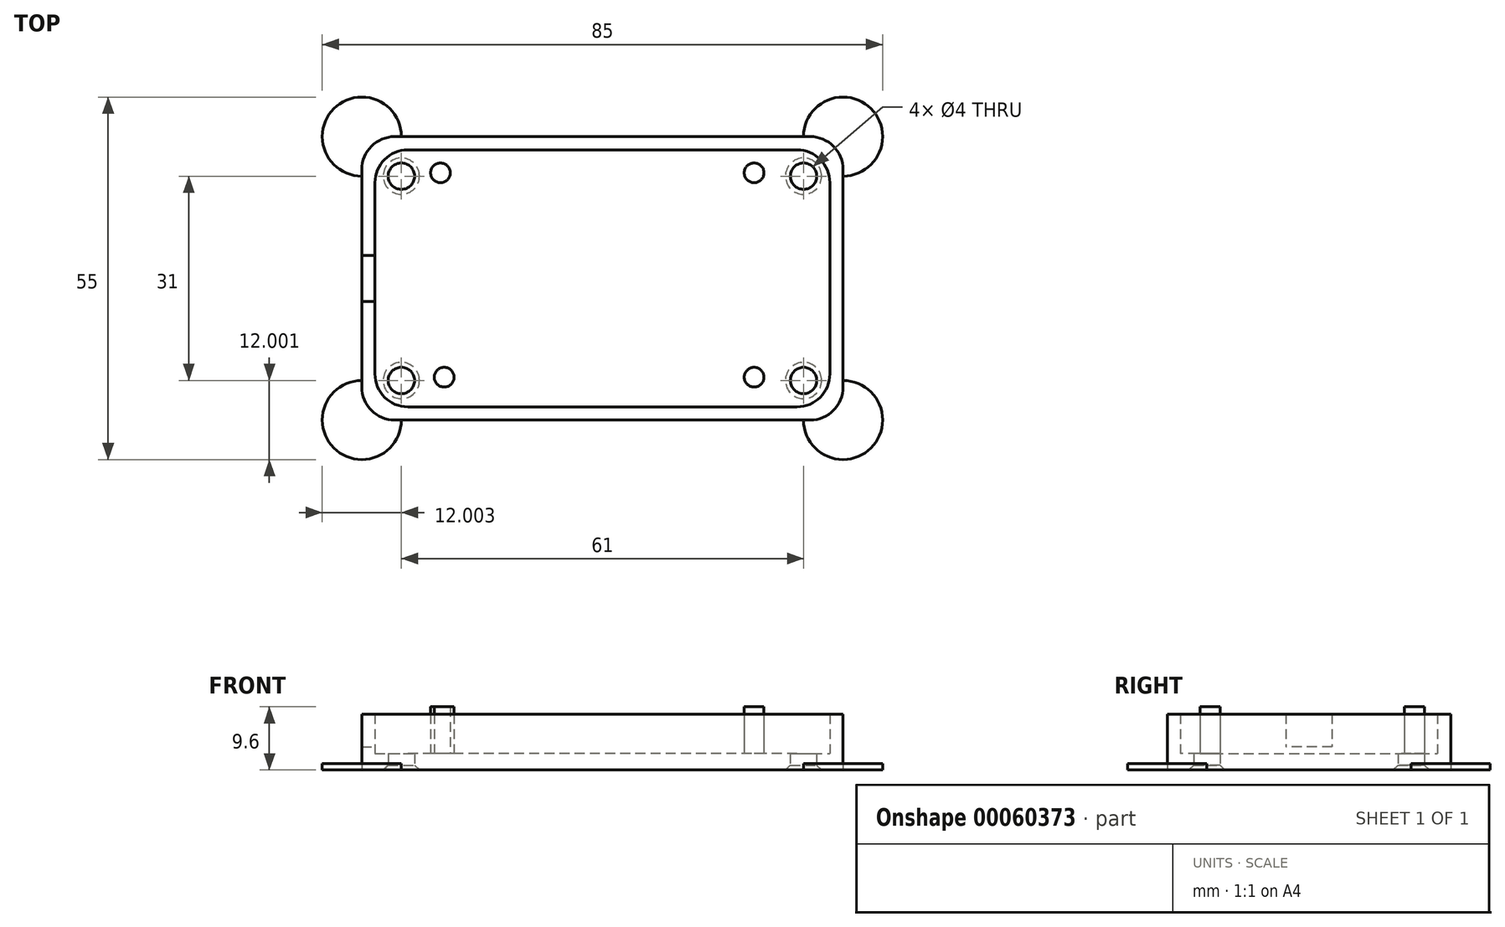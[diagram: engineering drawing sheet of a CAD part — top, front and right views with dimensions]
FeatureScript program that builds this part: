
annotation { "Feature Type Name" : "Feature", "Feature Type Description" : "" }
export const myFeature = defineFeature(function(context is Context, id is Id, definition is map)
    precondition{}
    {
        {
            var Q0;
            Q0=qCreatedBy(makeId("Top.planeOp"),FACE);
            var sketch = newSketch(context, id + "F0", { "sketchPlane" : qUnion([Q0])});
            skLineSegment(sketch, "E0.bottom", {"start": v(-6.76, 68.41) * mm, "end": v(52.24, 68.41) * mm});
            skLineSegment(sketch, "E0.top", {"start": v(-6.76, 29.41) * mm, "end": v(52.24, 29.41) * mm});
            skLineSegment(sketch, "E0.left", {"start": v(-11.76, 63.41) * mm, "end": v(-11.76, 34.41) * mm});
            skLineSegment(sketch, "E0.right", {"start": v(57.24, 63.41) * mm, "end": v(57.24, 34.41) * mm});
            skCircle(sketch, "E1", {"center": v(-7.76, 64.41) * mm, "radius": 1.5 * mm, "construction": true});
            skCircle(sketch, "E2", {"center": v(-7.76, 33.41) * mm, "radius": 1.5 * mm, "construction": true});
            skCircle(sketch, "E3", {"center": v(53.24, 64.41) * mm, "radius": 1.5 * mm, "construction": true});
            skCircle(sketch, "E4", {"center": v(53.24, 33.41) * mm, "radius": 1.5 * mm, "construction": true});
            skCircle(sketch, "E5.0", {"center": v(53.24, 33.41) * mm, "radius": 2 * mm});
            skCircle(sketch, "E6.0", {"center": v(53.24, 64.41) * mm, "radius": 2 * mm});
            skCircle(sketch, "E7.0", {"center": v(-7.76, 64.41) * mm, "radius": 2 * mm});
            skCircle(sketch, "E8.0", {"center": v(-7.76, 33.41) * mm, "radius": 2 * mm});
            skPoint(sketch, "E9", {"position": v(-1.26, 33.91) * mm});
            skLineSegment(sketch, "E10.0", {"start": v(-13.76, 65.41) * mm, "end": v(-13.76, 32.41) * mm});
            skLineSegment(sketch, "E10.1", {"start": v(-8.76, 70.41) * mm, "end": v(54.24, 70.41) * mm});
            skLineSegment(sketch, "E10.2", {"start": v(59.24, 65.41) * mm, "end": v(59.24, 32.41) * mm});
            skLineSegment(sketch, "E10.3", {"start": v(-8.76, 27.41) * mm, "end": v(54.24, 27.41) * mm});
            skPoint(sketch, "E11", {"position": v(-13.76, 52.41) * mm});
            skPoint(sketch, "E12", {"position": v(-13.76, 45.41) * mm});
            skLineSegment(sketch, "E13", {"start": v(-13.76, 52.41) * mm, "end": v(-11.76, 52.41) * mm});
            skLineSegment(sketch, "E14", {"start": v(-13.76, 45.41) * mm, "end": v(-11.76, 45.41) * mm});
            skPoint(sketch, "E15", {"position": v(-1.82, 64.91) * mm});
            skPoint(sketch, "E16", {"position": v(45.74, 33.91) * mm});
            skPoint(sketch, "E17", {"position": v(45.74, 64.91) * mm});
            skCircle(sketch, "E18", {"center": v(-1.26, 33.91) * mm, "radius": 1.5 * mm});
            skCircle(sketch, "E19", {"center": v(-1.82, 64.91) * mm, "radius": 1.5 * mm});
            skCircle(sketch, "E20", {"center": v(45.74, 64.91) * mm, "radius": 1.5 * mm});
            skCircle(sketch, "E21", {"center": v(45.74, 33.91) * mm, "radius": 1.5 * mm});
            skArc(sketch, "E22", {"start": v(59.24, 64.41) * mm, "mid": v(63.49, 74.65) * mm, "end": v(53.24, 70.41) * mm});
            skArc(sketch, "E23", {"start": v(53.24, 27.41) * mm, "mid": v(63.49, 23.17) * mm, "end": v(59.24, 33.41) * mm});
            skArc(sketch, "E24", {"start": v(-7.76, 70.41) * mm, "mid": v(-18, 74.65) * mm, "end": v(-13.76, 64.41) * mm});
            skArc(sketch, "E25", {"start": v(-13.76, 33.41) * mm, "mid": v(-18, 23.17) * mm, "end": v(-7.76, 27.41) * mm});
            skPoint(sketch, "E26.visualSharp", {"position": v(57.24, 68.41) * mm});
            skArc(sketch, "E26.filletArc", {"start": v(57.24, 63.41) * mm, "mid": v(55.78, 66.95) * mm, "end": v(52.24, 68.41) * mm});
            skArc(sketch, "E27.filletArc", {"start": v(59.24, 65.41) * mm, "mid": v(57.78, 68.95) * mm, "end": v(54.24, 70.41) * mm});
            skPoint(sketch, "E28.visualSharp", {"position": v(-11.76, 68.41) * mm});
            skArc(sketch, "E28.filletArc", {"start": v(-6.76, 68.41) * mm, "mid": v(-10.3, 66.95) * mm, "end": v(-11.76, 63.41) * mm});
            skArc(sketch, "E29.filletArc", {"start": v(-8.76, 70.41) * mm, "mid": v(-12.3, 68.95) * mm, "end": v(-13.76, 65.41) * mm});
            skPoint(sketch, "E30.visualSharp", {"position": v(-11.76, 29.41) * mm});
            skArc(sketch, "E30.filletArc", {"start": v(-11.76, 34.41) * mm, "mid": v(-10.3, 30.88) * mm, "end": v(-6.76, 29.41) * mm});
            skArc(sketch, "E31.filletArc", {"start": v(-13.76, 32.41) * mm, "mid": v(-12.3, 28.88) * mm, "end": v(-8.76, 27.41) * mm});
            skPoint(sketch, "E32.visualSharp", {"position": v(57.24, 29.41) * mm});
            skArc(sketch, "E32.filletArc", {"start": v(52.24, 29.41) * mm, "mid": v(55.78, 30.88) * mm, "end": v(57.24, 34.41) * mm});
            skArc(sketch, "E33.filletArc", {"start": v(54.24, 27.41) * mm, "mid": v(57.78, 28.88) * mm, "end": v(59.24, 32.41) * mm});
            skSolve(sketch);
        }
        {
            var Q0;
            {var subQ0=sQuery(id+"F0.wireOp",EDGE,"E0.bottom");Q0=makeQuery(id+"F0.imprint","IMPRINT",FACE,{"disambiguationData":[TD([[makeQuery(id+"F0.imprint","IMPRINT",EDGE,{"derivedFrom":subQ0}),-1.0]])]});}
            var Q1;
            {var subQ5=sQuery(id+"F0.wireOp",EDGE,"E0.bottom");Q1=makeQuery(id+"F0.imprint","IMPRINT",FACE,{"disambiguationData":[TD([[makeQuery(id+"F0.imprint","IMPRINT",EDGE,{"derivedFrom":subQ5}),1.0]])]});}
            var Q2;
            Q2=makeQuery(id+"F0.imprint","IMPRINT",FACE,{"disambiguationData":[TD([[makeQuery(id+"F0.imprint","IMPRINT",EDGE,{"derivedFrom":sQuery(id+"F0.wireOp",EDGE,"E18")}),1.0]])]});
            var Q3;
            Q3=makeQuery(id+"F0.imprint","IMPRINT",FACE,{"disambiguationData":[TD([[makeQuery(id+"F0.imprint","IMPRINT",EDGE,{"derivedFrom":sQuery(id+"F0.wireOp",EDGE,"E21")}),1.0]])]});
            var Q4;
            Q4=makeQuery(id+"F0.imprint","IMPRINT",FACE,{"disambiguationData":[TD([[makeQuery(id+"F0.imprint","IMPRINT",EDGE,{"derivedFrom":sQuery(id+"F0.wireOp",EDGE,"E20")}),1.0]])]});
            var Q5;
            Q5=makeQuery(id+"F0.imprint","IMPRINT",FACE,{"disambiguationData":[TD([[makeQuery(id+"F0.imprint","IMPRINT",EDGE,{"derivedFrom":sQuery(id+"F0.wireOp",EDGE,"E19")}),1.0]])]});
            var Q6;
            {var subQ0=sQuery(id+"F0.wireOp",EDGE,"E13");Q6=makeQuery(id+"F0.imprint","IMPRINT",FACE,{"disambiguationData":[TD([[makeQuery(id+"F0.imprint","IMPRINT",EDGE,{"derivedFrom":subQ0}),-1.0]])]});}
            extrude(context, id + "F1", {"entities" : qUnion([Q0, Q1, Q2, Q3, Q4, Q5, Q6]), "depth" : 2.5 * mm});
        }
        {
            var Q0;
            {var subQ5=sQuery(id+"F0.wireOp",EDGE,"E0.bottom");Q0=makeQuery(id+"F0.imprint","IMPRINT",FACE,{"disambiguationData":[TD([[makeQuery(id+"F0.imprint","IMPRINT",EDGE,{"derivedFrom":subQ5}),1.0]])]});}
            extrude(context, id + "F2", {"entities" : qUnion([Q0]), "operationType" : NewBodyOperationType.ADD, "depth" : 8.5 * mm});
        }
        {
            var Q0;
            Q0=makeQuery(id+"F0.imprint","IMPRINT",FACE,{"disambiguationData":[TD([[makeQuery(id+"F0.imprint","IMPRINT",EDGE,{"derivedFrom":sQuery(id+"F0.wireOp",EDGE,"E19")}),1.0]])]});
            var Q1;
            Q1=makeQuery(id+"F0.imprint","IMPRINT",FACE,{"disambiguationData":[TD([[makeQuery(id+"F0.imprint","IMPRINT",EDGE,{"derivedFrom":sQuery(id+"F0.wireOp",EDGE,"E18")}),1.0]])]});
            var Q2;
            Q2=makeQuery(id+"F0.imprint","IMPRINT",FACE,{"disambiguationData":[TD([[makeQuery(id+"F0.imprint","IMPRINT",EDGE,{"derivedFrom":sQuery(id+"F0.wireOp",EDGE,"E21")}),1.0]])]});
            var Q3;
            Q3=makeQuery(id+"F0.imprint","IMPRINT",FACE,{"disambiguationData":[TD([[makeQuery(id+"F0.imprint","IMPRINT",EDGE,{"derivedFrom":sQuery(id+"F0.wireOp",EDGE,"E20")}),1.0]])]});
            extrude(context, id + "F3", {"entities" : qUnion([Q0, Q1, Q2, Q3]), "operationType" : NewBodyOperationType.ADD, "depth" : 9.6 * mm});
        }
        {
            var Q0;
            {var subQ0=sQuery(id+"F0.wireOp",EDGE,"E13");Q0=makeQuery(id+"F0.imprint","IMPRINT",FACE,{"disambiguationData":[TD([[makeQuery(id+"F0.imprint","IMPRINT",EDGE,{"derivedFrom":subQ0}),-1.0]])]});}
            extrude(context, id + "F4", {"entities" : qUnion([Q0]), "operationType" : NewBodyOperationType.ADD, "depth" : 3.5 * mm});
        }
        {
            var Q0;
            Q0=sQuery(id+"F0.wireOp",VERTEX,"E3.center");
            var Q1;
            Q1=sQuery(id+"F0.wireOp",VERTEX,"E4.center");
            var Q2;
            Q2=sQuery(id+"F0.wireOp",VERTEX,"E2.center");
            var Q3;
            Q3=sQuery(id+"F0.wireOp",VERTEX,"E1.center");
            var Q4;
            Q4=makeQuery(id+"F1.opExtrude","SWEPT_BODY",BODY,{"disambiguationData":[OSD([sQuery(id+"F0.wireOp",EDGE,"E5.0"),sQuery(id+"F0.wireOp",EDGE,"E6.0"),sQuery(id+"F0.wireOp",EDGE,"E7.0"),sQuery(id+"F0.wireOp",EDGE,"E8.0"),sQuery(id+"F0.wireOp",EDGE,"E10.0"),sQuery(id+"F0.wireOp",EDGE,"E10.1"),sQuery(id+"F0.wireOp",EDGE,"E10.2"),sQuery(id+"F0.wireOp",EDGE,"E10.3")])]});
            hole(context, id + "F5", {"style" : HoleStyle.C_SINK, "holeDiameter" : 3 * mm, "cSinkDiameter" : 5.5 * mm, "endStyle" : HoleEndStyle.THROUGH, "oppositeDirection" : true, "locations" : qUnion([Q0, Q1, Q2, Q3]), "scope" : qUnion([Q4]), "cSinkAngle" : 90 * degree});
        }
        {
            var Q0;
            {var subQ3=sQuery(id+"F0.wireOp",EDGE,"E24");Q0=makeQuery(id+"F0.imprint","IMPRINT",FACE,{"disambiguationData":[TD([[makeQuery(id+"F0.imprint","IMPRINT",EDGE,{"derivedFrom":subQ3}),1.0]])]});}
            var Q1;
            {var subQ3=sQuery(id+"F0.wireOp",EDGE,"E22");Q1=makeQuery(id+"F0.imprint","IMPRINT",FACE,{"disambiguationData":[TD([[makeQuery(id+"F0.imprint","IMPRINT",EDGE,{"derivedFrom":subQ3}),1.0]])]});}
            var Q2;
            {var subQ3=sQuery(id+"F0.wireOp",EDGE,"E23");Q2=makeQuery(id+"F0.imprint","IMPRINT",FACE,{"disambiguationData":[TD([[makeQuery(id+"F0.imprint","IMPRINT",EDGE,{"derivedFrom":subQ3}),1.0]])]});}
            var Q3;
            {var subQ3=sQuery(id+"F0.wireOp",EDGE,"E25");Q3=makeQuery(id+"F0.imprint","IMPRINT",FACE,{"disambiguationData":[TD([[makeQuery(id+"F0.imprint","IMPRINT",EDGE,{"derivedFrom":subQ3}),1.0]])]});}
            extrude(context, id + "F6", {"entities" : qUnion([Q0, Q1, Q2, Q3]), "operationType" : NewBodyOperationType.ADD, "depth" : 1 * mm});
        }
    });
